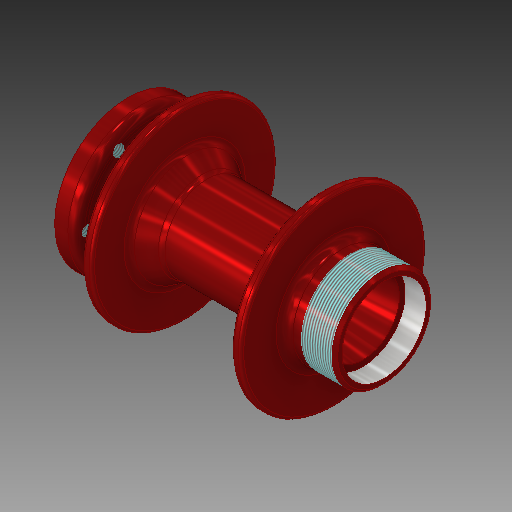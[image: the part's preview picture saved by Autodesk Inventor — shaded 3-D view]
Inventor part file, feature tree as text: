
AUTODESK INVENTOR PART (.ipt)
format: ipt  version: 2019.2 (Build 232265000, 265)  size: 409,600 bytes
history: native  units: mm
features: revolve x1, fillet x1, thread x1, chamfer x1, hole x1, pattern_circular x1, sketch x1
ambient origin geometry x8: Origin, YZ Plane, XZ Plane, XY Plane, X Axis, Y Axis, Z Axis, Center Point
bodies: Solid1 (feature_tree)
feature tree (7):
  revolve  "Revolution1"  [1 undecoded]
  fillet  "Fillet6"  Radius=16.65mm
  thread  "Thread1"  [1 undecoded]
  chamfer  "Chamfer2"  Distance=9.0mm
  hole  "Hole2"  [1 undecoded]
  pattern_circular  "Circular Pattern2"  [2 undecoded]
  sketch  "Sketch6"  dims[d29=90.0deg d53=9.0mm d54=16.65mm d72=3.0mm d73=1.0mm d77=9.0mm d78=7.5mm d83=5.0mm d84=7.0mm d89=12.0mm d90=0.0mm d91=1.0mm d92=2.0mm d93=45.0deg d94=22.0mm d95=4.134mm d96=10.0mm d97=4.0mm d98=2.0mm d99=90.0deg d100=8.0mm d101=20.594885mm d105=60.0mm d106=360.0deg d119=56.5mm d120=93.5mm d121=39.75mm d122=17.85mm d123=10.0mm d124=15.0mm d125=33.0mm d126=3.5mm d127=3.5mm d129=5.0mm d130=7.0mm d131=5.0mm d132=19.0mm d133=17.5mm d134=2.0mm d135=38.2mm d137=7.5mm d139=2.0mm d140=26.0mm d141=136.0mm]
note: 5 required parameter values undecoded (feature->parameter linkage not recoverable at this tier; creation-order binding heuristic only, values carry confidence <= 0.55)